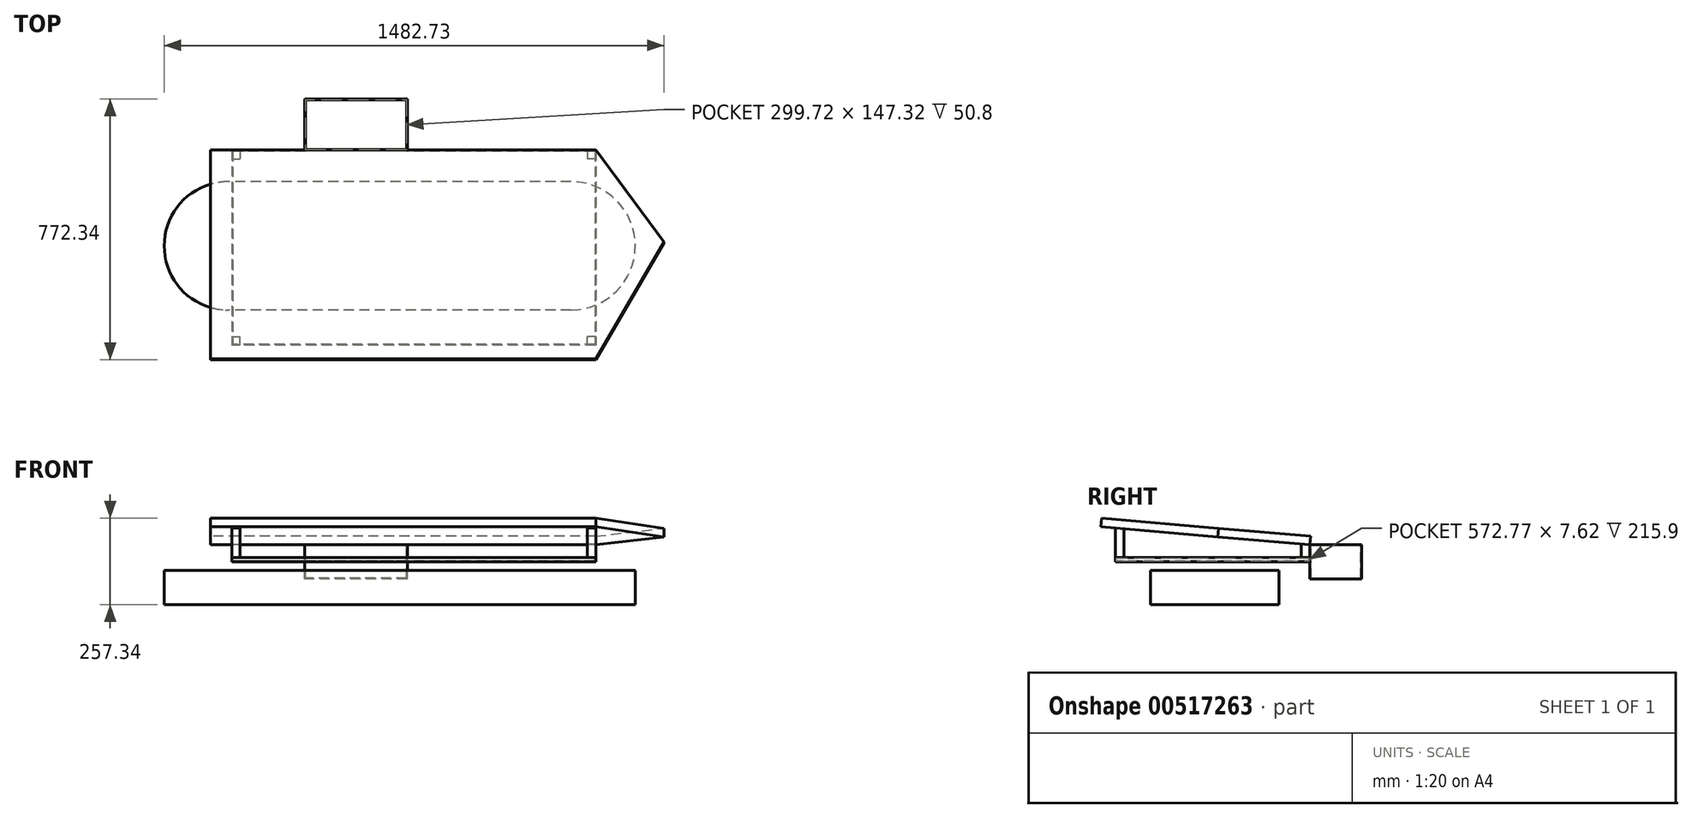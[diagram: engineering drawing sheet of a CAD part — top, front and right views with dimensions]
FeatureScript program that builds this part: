
annotation { "Feature Type Name" : "Feature", "Feature Type Description" : "" }
export const myFeature = defineFeature(function(context is Context, id is Id, definition is map)
    precondition{}
    {
        {
            var Q0;
            Q0=qCreatedBy(makeId("Top.planeOp"),FACE);
            var sketch = newSketch(context, id + "F0", { "sketchPlane" : qUnion([Q0])});
            skLineSegment(sketch, "E0", {"start": v(454.03, 257.18) * mm, "end": v(454.03, -320.67) * mm});
            skLineSegment(sketch, "E1", {"start": v(454.03, -320.68) * mm, "end": v(-625.48, -320.68) * mm});
            skLineSegment(sketch, "E2", {"start": v(454.03, 257.18) * mm, "end": v(-625.48, 257.17) * mm});
            skLineSegment(sketch, "E3", {"start": v(-625.48, 257.17) * mm, "end": v(-625.48, -320.68) * mm});
            skSolve(sketch);
        }
        {
            var Q0;
            Q0 = qSketchRegion(id + "F0", true);
            extrude(context, id + "F1", {"entities" : qUnion([Q0]), "oppositeDirection" : true, "depth" : 12.7 * mm, "offsetDistance" : 25.4 * mm});
        }
        {
            var Q0;
            Q0=qCreatedBy(makeId("Top.planeOp"),FACE);
            cPlane(context, id + "F2", {"entities" : qUnion([Q0]), "cplaneType" : CPlaneType.OFFSET, "offset" : 38.1 * mm, "width" : 152.4 * mm, "height" : 152.4 * mm});
        }
        {
            var Q0;
            Q0=qCreatedBy(id+"F2.planeOp",FACE);
            var sketch = newSketch(context, id + "F3", { "sketchPlane" : qUnion([Q0])});
            skLineSegment(sketch, "E4", {"start": v(454.03, 257.18) * mm, "end": v(-625.48, 257.18) * mm, "construction": true});
            skSolve(sketch);
        }
        {
            var Q0;
            Q0=sQuery(id+"F3.wireOp",EDGE,"E4");
            cPlane(context, id + "F4", {"entities" : qUnion([Q0]), "cplaneType" : CPlaneType.LINE_ANGLE, "offset" : 25.4 * mm, "angle" : 95 * degree, "width" : 152.4 * mm, "height" : 152.4 * mm});
        }
        {
            var Q0;
            Q0=qCreatedBy(id+"F4.planeOp",FACE);
            var sketch = newSketch(context, id + "F5", { "sketchPlane" : qUnion([Q0])});
            skLineSegment(sketch, "E5.bottom", {"start": v(454.03, 252.88) * mm, "end": v(-688.98, 252.88) * mm});
            skLineSegment(sketch, "E5.top", {"start": v(454.03, -369.42) * mm, "end": v(-688.97, -369.42) * mm});
            skLineSegment(sketch, "E5.left", {"start": v(454.03, 252.88) * mm, "end": v(454.03, -369.42) * mm});
            skLineSegment(sketch, "E5.right", {"start": v(-688.98, 252.88) * mm, "end": v(-688.97, -369.42) * mm});
            skLineSegment(sketch, "E6", {"start": v(454.03, 252.88) * mm, "end": v(657.23, -21.44) * mm});
            skLineSegment(sketch, "E7", {"start": v(657.23, -21.44) * mm, "end": v(454.02, -369.42) * mm});
            skLineSegment(sketch, "E8", {"start": v(657.23, -21.44) * mm, "end": v(454.03, -21.44) * mm});
            skSolve(sketch);
        }
        {
            var Q0;
            Q0 = qSketchRegion(id + "F5", true);
            extrude(context, id + "F6", {"entities" : qUnion([Q0]), "depth" : 25.4 * mm, "offsetDistance" : 25.4 * mm});
        }
        {
            var Q0;
            Q0=makeQuery(id+"F1.opExtrude","CAP_FACE",FACE,{"disambiguationData":[OSD([sQuery(id+"F0.wireOp",EDGE,"9ksEp5GQ-oAJT-P4iE-0mX8-ivWTJKNYp43P"),sQuery(id+"F0.wireOp",EDGE,"OuI4fd9M-uFcz-1QnF-mgBD-I5K9x2dfRTDU"),sQuery(id+"F0.wireOp",EDGE,"E0"),sQuery(id+"F0.wireOp",EDGE,"E1"),sQuery(id+"F0.wireOp",EDGE,"YYVQHE9j-lWI6-javn-eY3g-upZKrsheIzAp"),sQuery(id+"F0.wireOp",EDGE,"7gQHpipr-8uyv-p4V5-9LbC-UoGURH3aDsHJ")])],"isStart":false});
            cPlane(context, id + "F7", {"entities" : qUnion([Q0]), "cplaneType" : CPlaneType.OFFSET, "offset" : 25.4 * mm, "width" : 152.4 * mm, "height" : 152.4 * mm});
        }
        {
            var Q0;
            Q0=qCreatedBy(id+"F7.planeOp",FACE);
            var sketch = newSketch(context, id + "F8", { "sketchPlane" : qUnion([Q0])});
            skLineSegment(sketch, "E9.bottom", {"start": v(381, 215.9) * mm, "end": v(-635, 215.9) * mm});
            skLineSegment(sketch, "E9.top", {"start": v(381, -165.1) * mm, "end": v(-635, -165.1) * mm});
            skArc(sketch, "E10", {"start": v(381, 215.9) * mm, "mid": v(571.5, 25.4) * mm, "end": v(381, -165.1) * mm});
            skArc(sketch, "E11", {"start": v(-635, 215.9) * mm, "mid": v(-825.5, 25.4) * mm, "end": v(-635, -165.1) * mm});
            skSolve(sketch);
        }
        {
            var Q0;
            Q0 = qSketchRegion(id + "F8", true);
            extrude(context, id + "F9", {"entities" : qUnion([Q0]), "depth" : 101.6 * mm, "offsetDistance" : 25.4 * mm});
        }
        {
            var Q0;
            Q0=qCreatedBy(id+"F2.planeOp",FACE);
            var sketch = newSketch(context, id + "F10", { "sketchPlane" : qUnion([Q0])});
            skLineSegment(sketch, "E12.bottom", {"start": v(-104.78, 257.18) * mm, "end": v(-409.58, 257.18) * mm});
            skLineSegment(sketch, "E12.top", {"start": v(-104.78, 409.58) * mm, "end": v(-409.58, 409.58) * mm});
            skLineSegment(sketch, "E12.left", {"start": v(-104.78, 257.18) * mm, "end": v(-104.78, 409.58) * mm});
            skLineSegment(sketch, "E12.right", {"start": v(-409.58, 257.18) * mm, "end": v(-409.58, 409.58) * mm});
            skSolve(sketch);
        }
        {
            var Q0;
            Q0 = qSketchRegion(id + "F10", true);
            extrude(context, id + "F11", {"entities" : qUnion([Q0]), "operationType" : NewBodyOperationType.ADD, "oppositeDirection" : true, "depth" : 101.6 * mm, "offsetDistance" : 25.4 * mm});
        }
        {
            var Q0;
            Q0 = qConstructionFilter(qBodyType(qCreatedBy(id + "F10" ,EDGE), BodyType.WIRE), ConstructionObject.NO);
            extrude(context, id + "F12", {"bodyType" : ToolBodyType.SURFACE, "surfaceEntities" : qUnion([Q0]), "depth" : 25.4 * mm, "offsetDistance" : 25.4 * mm});
        }
        {
            var Q0;
            Q0=makeQuery(id+"F11.opExtrude","CAP_FACE",FACE,{"disambiguationData":[OSD([sQuery(id+"F10.wireOp",EDGE,"E12.bottom"),sQuery(id+"F10.wireOp",EDGE,"E12.top"),sQuery(id+"F10.wireOp",EDGE,"E12.left"),sQuery(id+"F10.wireOp",EDGE,"E12.right")])],"isStart":true});
            shell(context, id + "F13", {"entities" : qUnion([Q0]), "thickness" : 2.54 * mm});
        }
        {
            var Q0;
            Q0=makeQuery(id+"F1.opExtrude","CAP_FACE",FACE,{"disambiguationData":[OSD([sQuery(id+"F0.wireOp",EDGE,"E0"),sQuery(id+"F0.wireOp",EDGE,"E1"),sQuery(id+"F0.wireOp",EDGE,"E2"),sQuery(id+"F0.wireOp",EDGE,"E3")])],"isStart":true});
            var sketch = newSketch(context, id + "F14", { "sketchPlane" : qUnion([Q0])});
            skLineSegment(sketch, "E13.bottom", {"start": v(454.03, 257.18) * mm, "end": v(428.63, 257.18) * mm});
            skLineSegment(sketch, "E13.top", {"start": v(454.03, 231.78) * mm, "end": v(428.63, 231.78) * mm});
            skLineSegment(sketch, "E13.left", {"start": v(454.03, 257.18) * mm, "end": v(454.03, 231.78) * mm});
            skLineSegment(sketch, "E13.right", {"start": v(428.63, 257.18) * mm, "end": v(428.63, 231.78) * mm});
            skLineSegment(sketch, "E14.bottom", {"start": v(-625.48, 257.17) * mm, "end": v(-600.08, 257.17) * mm});
            skLineSegment(sketch, "E14.top", {"start": v(-625.48, 231.77) * mm, "end": v(-600.08, 231.77) * mm});
            skLineSegment(sketch, "E14.left", {"start": v(-625.48, 257.17) * mm, "end": v(-625.48, 231.77) * mm});
            skLineSegment(sketch, "E14.right", {"start": v(-600.08, 257.17) * mm, "end": v(-600.08, 231.77) * mm});
            skLineSegment(sketch, "E15.bottom", {"start": v(-625.48, -320.68) * mm, "end": v(-600.08, -320.68) * mm});
            skLineSegment(sketch, "E15.top", {"start": v(-625.48, -295.28) * mm, "end": v(-600.08, -295.28) * mm});
            skLineSegment(sketch, "E15.left", {"start": v(-625.48, -320.68) * mm, "end": v(-625.48, -295.28) * mm});
            skLineSegment(sketch, "E15.right", {"start": v(-600.08, -320.68) * mm, "end": v(-600.08, -295.28) * mm});
            skLineSegment(sketch, "E16.bottom", {"start": v(454.03, -320.67) * mm, "end": v(428.63, -320.67) * mm});
            skLineSegment(sketch, "E16.top", {"start": v(454.03, -295.27) * mm, "end": v(428.63, -295.27) * mm});
            skLineSegment(sketch, "E16.left", {"start": v(454.03, -320.67) * mm, "end": v(454.03, -295.27) * mm});
            skLineSegment(sketch, "E16.right", {"start": v(428.63, -320.67) * mm, "end": v(428.63, -295.27) * mm});
            skSolve(sketch);
        }
        {
            var Q0;
            Q0 = qSketchRegion(id + "F14", true);
            extrude(context, id + "F15", {"entities" : qUnion([Q0]), "endBound" : BoundingType.UP_TO_NEXT, "depth" : 25.4 * mm, "offsetDistance" : 25.4 * mm});
        }
    });
